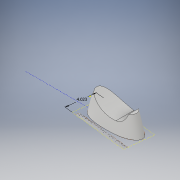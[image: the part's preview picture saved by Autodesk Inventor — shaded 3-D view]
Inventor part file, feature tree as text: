
AUTODESK INVENTOR PART (.ipt)
format: ipt  version: 2018 (Build 220112000, 112)  size: 1,610,240 bytes
history: native  units: in
note: dims shown in document units (in); Inventor stores cm internally (conversion verified against a paired STEP export)
features: sketch x6, other x4, plane x2, surface_op x1, loft x1, extrude x1
ambient origin geometry x8: Origin, YZ Plane, XZ Plane, XY Plane, X Axis, Y Axis, Z Axis, Center Point
bodies: Solid1 (feature_tree)
feature tree (15):
  sketch  "Sketch Side Profile"  dims[d58=0.0in d59=90.0deg]
  sketch  "Sketch2"  dims[d14=7.5in d17=8.8089in]
  sketch  "Sketch Base Profile"  dims[d60=0.0in d61=90.0deg d67=3.0in d68=0.0in]
  plane  "Work Plane 1.5"
  sketch  "Sketch4"  dims[d39=4.0225in d53=1.5in]
  sketch  "Sketch5"  dims[d54=3.5in]
  plane  "Work Plane2"
  surface_op  "Sculpt1"
  other  "Image1"
  other  "Image2"
  sketch  "Sketch6"  dims[d56=0.0in d57=90.0deg]
  other  "Srf1"
  other  "Srf2"
  loft  "LoftSrf1"
  extrude  "ExtrusionSrf1"  Depth=1.5in
